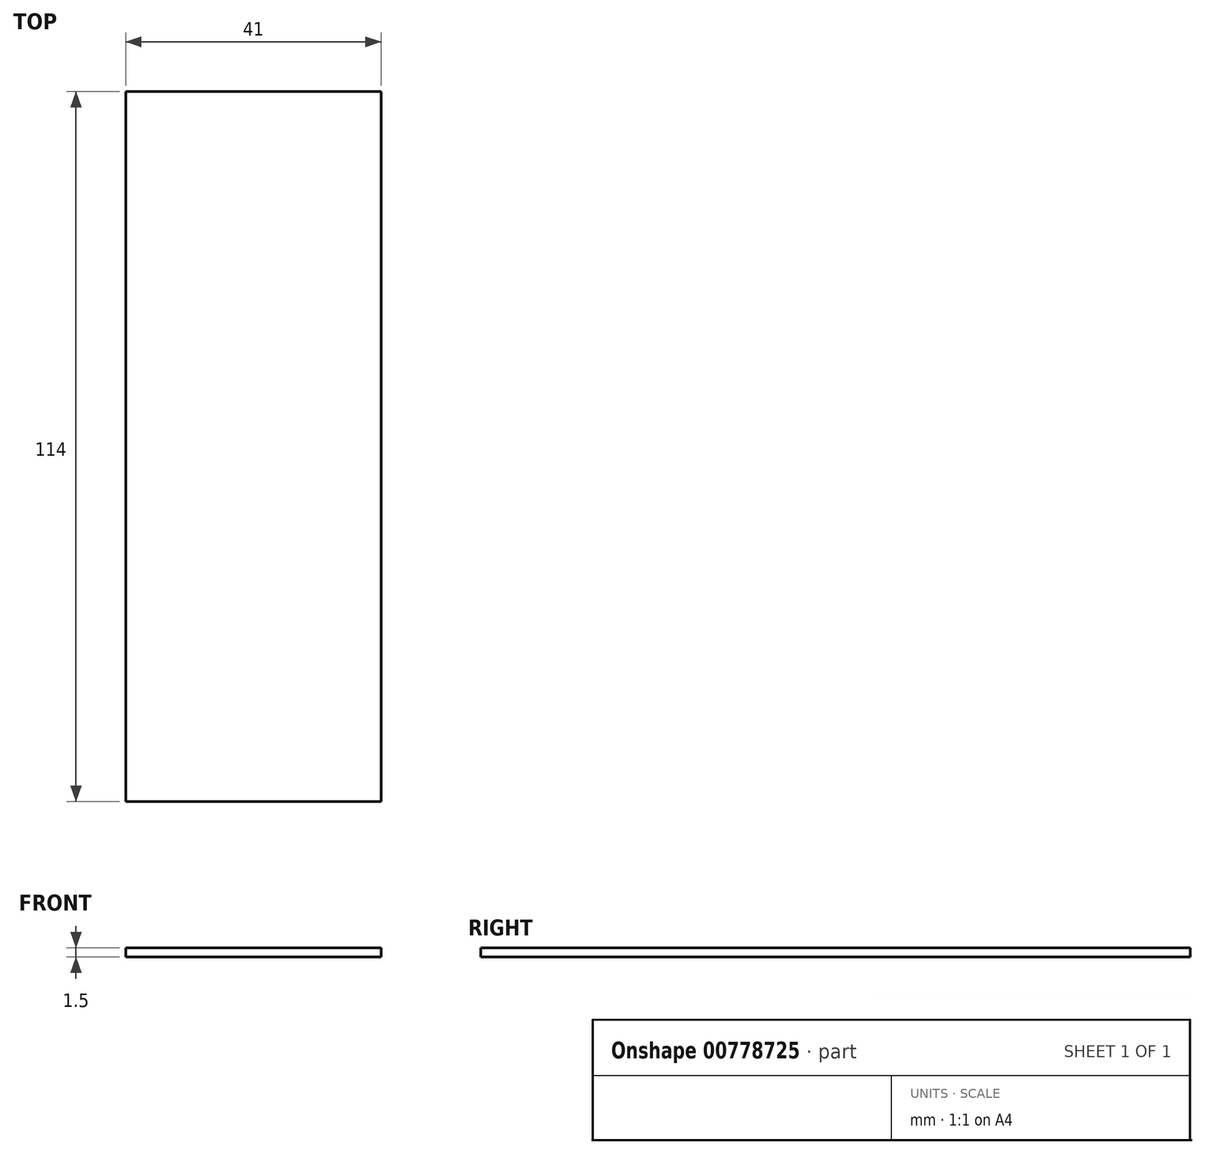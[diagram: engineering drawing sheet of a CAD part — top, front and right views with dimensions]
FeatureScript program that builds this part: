
annotation { "Feature Type Name" : "Feature", "Feature Type Description" : "" }
export const myFeature = defineFeature(function(context is Context, id is Id, definition is map)
    precondition{}
    {
        {
            var Q0;
            Q0=qCreatedBy(makeId("Top.planeOp"),FACE);
            var sketch = newSketch(context, id + "F0", { "sketchPlane" : qUnion([Q0])});
            skLineSegment(sketch, "E0.bottom", {"start": v(20.5, -57) * mm, "end": v(-20.5, -57) * mm});
            skLineSegment(sketch, "E0.top", {"start": v(20.5, 57) * mm, "end": v(-20.5, 57) * mm});
            skLineSegment(sketch, "E0.left", {"start": v(20.5, -57) * mm, "end": v(20.5, 57) * mm});
            skLineSegment(sketch, "E0.right", {"start": v(-20.5, -57) * mm, "end": v(-20.5, 57) * mm});
            skPoint(sketch, "E0.middle", {"position": v(0, 0) * mm});
            skSolve(sketch);
        }
        {
            var Q0;
            Q0=makeQuery(id+"F0.imprint","IMPRINT",FACE,{"disambiguationData":[TD([[makeQuery(id+"F0.imprint","IMPRINT",EDGE,{"derivedFrom":sQuery(id+"F0.wireOp",EDGE,"E0.bottom")}),-1.0]])]});
            extrude(context, id + "F1", {"entities" : qUnion([Q0]), "depth" : 1.5 * mm, "offsetDistance" : 25 * mm});
        }
    });
